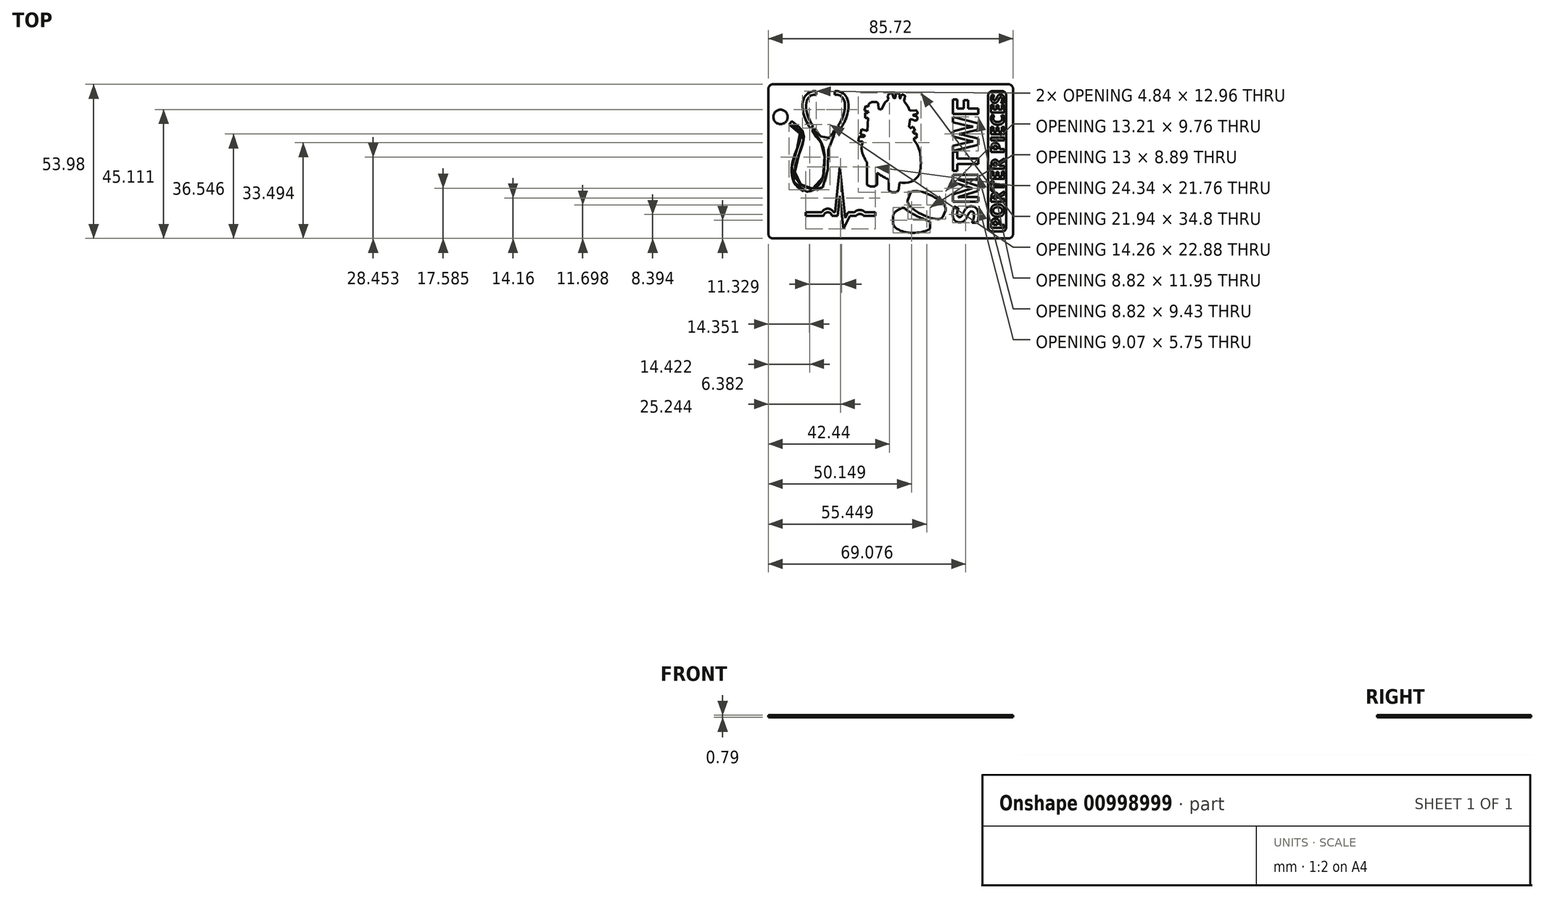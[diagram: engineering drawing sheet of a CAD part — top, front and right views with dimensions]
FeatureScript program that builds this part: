
annotation { "Feature Type Name" : "Feature", "Feature Type Description" : "" }
export const myFeature = defineFeature(function(context is Context, id is Id, definition is map)
    precondition{}
    {
        {
            var Q0;
            Q0=qCreatedBy(makeId("Top.planeOp"),FACE);
            var sketch = newSketch(context, id + "F0", { "sketchPlane" : qUnion([Q0])});
            skLineSegment(sketch, "E0.bottom", {"start": v(42.86, 26.99) * mm, "end": v(-42.86, 26.99) * mm});
            skLineSegment(sketch, "E0.top", {"start": v(42.86, -26.99) * mm, "end": v(-42.86, -26.99) * mm});
            skLineSegment(sketch, "E0.left", {"start": v(42.86, 26.99) * mm, "end": v(42.86, -26.99) * mm});
            skLineSegment(sketch, "E0.right", {"start": v(-42.86, 26.99) * mm, "end": v(-42.86, -26.99) * mm});
            skPoint(sketch, "E0.middle", {"position": v(0, 0) * mm});
            skSolve(sketch);
        }
        {
            var Q0;
            Q0=makeQuery(id+"F0.imprint","IMPRINT",FACE,{"disambiguationData":[TD([[makeQuery(id+"F0.imprint","IMPRINT",EDGE,{"derivedFrom":sQuery(id+"F0.wireOp",EDGE,"E0.bottom")}),1.0]])]});
            extrude(context, id + "F1", {"entities" : qUnion([Q0]), "depth" : 0.8 * mm, "offsetDistance" : 25.4 * mm});
        }
        {
            var Q0;
            Q0=makeQuery(id+"F1.opExtrude","SWEPT_EDGE",EDGE,{"disambiguationData":[OSD([sQuery(id+"F0.wireOp",EDGE,"E0.bottom"),sQuery(id+"F0.wireOp",EDGE,"E0.left")])]});
            var Q1;
            Q1=makeQuery(id+"F1.opExtrude","SWEPT_EDGE",EDGE,{"disambiguationData":[OSD([sQuery(id+"F0.wireOp",EDGE,"E0.bottom"),sQuery(id+"F0.wireOp",EDGE,"E0.right")])]});
            var Q2;
            Q2=makeQuery(id+"F1.opExtrude","SWEPT_EDGE",EDGE,{"disambiguationData":[OSD([sQuery(id+"F0.wireOp",EDGE,"E0.top"),sQuery(id+"F0.wireOp",EDGE,"E0.right")])]});
            var Q3;
            Q3=makeQuery(id+"F1.opExtrude","SWEPT_EDGE",EDGE,{"disambiguationData":[OSD([sQuery(id+"F0.wireOp",EDGE,"E0.top"),sQuery(id+"F0.wireOp",EDGE,"E0.left")])]});
            fillet(context, id + "F2", {"entities" : qUnion([Q0, Q1, Q2, Q3]), "radius" : 1.59 * mm, "tangentPropagation" : true, "allowEdgeOverflow" : false});
        }
        {
            var Q0;
            Q0=makeQuery(id+"F1.opExtrude","CAP_FACE",FACE,{"disambiguationData":[OSD([sQuery(id+"F0.wireOp",EDGE,"E0.bottom"),sQuery(id+"F0.wireOp",EDGE,"E0.top"),sQuery(id+"F0.wireOp",EDGE,"E0.left"),sQuery(id+"F0.wireOp",EDGE,"E0.right")])],"isStart":false});
            var sketch = newSketch(context, id + "F3", { "sketchPlane" : qUnion([Q0])});
            skLineSegment(sketch, "E1.bottom", {"start": v(34.13, -24.6) * mm, "end": v(40.48, -24.6) * mm});
            skLineSegment(sketch, "E1.top", {"start": v(34.13, 24.6) * mm, "end": v(40.48, 24.6) * mm});
            skLineSegment(sketch, "E1.left", {"start": v(34.13, -24.6) * mm, "end": v(34.13, 24.6) * mm});
            skLineSegment(sketch, "E1.right", {"start": v(40.48, -24.6) * mm, "end": v(40.48, 24.6) * mm});
            skSolve(sketch);
        }
        {
            var Q0;
            Q0=makeQuery(id+"F3.imprint","IMPRINT",FACE,{"disambiguationData":[TD([[makeQuery(id+"F3.imprint","IMPRINT",EDGE,{"derivedFrom":sQuery(id+"F3.wireOp",EDGE,"E1.bottom")}),1.0]])]});
            extrude(context, id + "F4", {"entities" : qUnion([Q0]), "operationType" : NewBodyOperationType.REMOVE, "oppositeDirection" : true, "depth" : 0.4 * mm, "offsetDistance" : 25.4 * mm});
        }
        {
            var Q0;
            Q0=makeQuery(id+"F4.boolean.opBoolean","COPY",EDGE,{"derivedFrom":makeQuery(id+"F4.opExtrude","SWEPT_EDGE",EDGE,{"disambiguationData":[OSD([sQuery(id+"F3.wireOp",EDGE,"E1.bottom"),sQuery(id+"F3.wireOp",EDGE,"E1.left")])]})});
            var Q1;
            Q1=makeQuery(id+"F4.boolean.opBoolean","COPY",EDGE,{"derivedFrom":makeQuery(id+"F4.opExtrude","SWEPT_EDGE",EDGE,{"disambiguationData":[OSD([sQuery(id+"F3.wireOp",EDGE,"E1.bottom"),sQuery(id+"F3.wireOp",EDGE,"E1.right")])]})});
            var Q2;
            Q2=makeQuery(id+"F4.boolean.opBoolean","COPY",EDGE,{"derivedFrom":makeQuery(id+"F4.opExtrude","SWEPT_EDGE",EDGE,{"disambiguationData":[OSD([sQuery(id+"F3.wireOp",EDGE,"E1.top"),sQuery(id+"F3.wireOp",EDGE,"E1.right")])]})});
            var Q3;
            Q3=makeQuery(id+"F4.boolean.opBoolean","COPY",EDGE,{"derivedFrom":makeQuery(id+"F4.opExtrude","SWEPT_EDGE",EDGE,{"disambiguationData":[OSD([sQuery(id+"F3.wireOp",EDGE,"E1.top"),sQuery(id+"F3.wireOp",EDGE,"E1.left")])]})});
            fillet(context, id + "F5", {"entities" : qUnion([Q0, Q1, Q2, Q3]), "radius" : 1.59 * mm, "tangentPropagation" : true, "allowEdgeOverflow" : false});
        }
        {
            var Q0;
            Q0=makeQuery(id+"F4.boolean.opBoolean","COPY",FACE,{"derivedFrom":makeQuery(id+"F4.opExtrude","CAP_FACE",FACE,{"disambiguationData":[OSD([sQuery(id+"F3.wireOp",EDGE,"E1.bottom"),sQuery(id+"F3.wireOp",EDGE,"E1.top"),sQuery(id+"F3.wireOp",EDGE,"E1.left"),sQuery(id+"F3.wireOp",EDGE,"E1.right")])],"isStart":false})});
            var sketch = newSketch(context, id + "F6", { "sketchPlane" : qUnion([Q0])});
            skText(sketch, "E2", { "text": "PORTER PIECES", "fontName": "OpenSans-Bold.ttf"});
            const initialGuessF6  = {"E2": [0.03976, -0.02381, 0, 1, 0.00461]};
            skSetInitialGuess(sketch, initialGuessF6);
            skSolve(sketch);
        }
        {
            var Q0;
            Q0=makeQuery(id+"F6.imprint","IMPRINT",FACE,{"disambiguationData":[TD([[makeQuery(id+"F6.imprint","IMPRINT",EDGE,{"derivedFrom":sQuery(id+"F6.wireOp",EDGE,"E2.sketch_text.stroke-0")}),-1.0]])]});
            var Q1;
            Q1=makeQuery(id+"F6.imprint","IMPRINT",FACE,{"disambiguationData":[TD([[makeQuery(id+"F6.imprint","IMPRINT",EDGE,{"derivedFrom":sQuery(id+"F6.wireOp",EDGE,"E2.sketch_text.stroke-16")}),-1.0]])]});
            var Q2;
            Q2=makeQuery(id+"F6.imprint","IMPRINT",FACE,{"disambiguationData":[TD([[makeQuery(id+"F6.imprint","IMPRINT",EDGE,{"derivedFrom":sQuery(id+"F6.wireOp",EDGE,"E2.sketch_text.stroke-30")}),-1.0]])]});
            var Q3;
            Q3=makeQuery(id+"F6.imprint","IMPRINT",FACE,{"disambiguationData":[TD([[makeQuery(id+"F6.imprint","IMPRINT",EDGE,{"derivedFrom":sQuery(id+"F6.wireOp",EDGE,"E2.sketch_text.stroke-49")}),-1.0]])]});
            var Q4;
            Q4=makeQuery(id+"F6.imprint","IMPRINT",FACE,{"disambiguationData":[TD([[makeQuery(id+"F6.imprint","IMPRINT",EDGE,{"derivedFrom":sQuery(id+"F6.wireOp",EDGE,"E2.sketch_text.stroke-57")}),-1.0]])]});
            var Q5;
            Q5=makeQuery(id+"F6.imprint","IMPRINT",FACE,{"disambiguationData":[TD([[makeQuery(id+"F6.imprint","IMPRINT",EDGE,{"derivedFrom":sQuery(id+"F6.wireOp",EDGE,"E2.sketch_text.stroke-69")}),-1.0]])]});
            var Q6;
            Q6=makeQuery(id+"F6.imprint","IMPRINT",FACE,{"disambiguationData":[TD([[makeQuery(id+"F6.imprint","IMPRINT",EDGE,{"derivedFrom":sQuery(id+"F6.wireOp",EDGE,"E2.sketch_text.stroke-88")}),-1.0]])]});
            var Q7;
            Q7=makeQuery(id+"F6.imprint","IMPRINT",FACE,{"disambiguationData":[TD([[makeQuery(id+"F6.imprint","IMPRINT",EDGE,{"derivedFrom":sQuery(id+"F6.wireOp",EDGE,"E2.sketch_text.stroke-104")}),-1.0]])]});
            var Q8;
            Q8=makeQuery(id+"F6.imprint","IMPRINT",FACE,{"disambiguationData":[TD([[makeQuery(id+"F6.imprint","IMPRINT",EDGE,{"derivedFrom":sQuery(id+"F6.wireOp",EDGE,"E2.sketch_text.stroke-108")}),-1.0]])]});
            var Q9;
            Q9=makeQuery(id+"F6.imprint","IMPRINT",FACE,{"disambiguationData":[TD([[makeQuery(id+"F6.imprint","IMPRINT",EDGE,{"derivedFrom":sQuery(id+"F6.wireOp",EDGE,"E2.sketch_text.stroke-120")}),-1.0]])]});
            var Q10;
            Q10=makeQuery(id+"F6.imprint","IMPRINT",FACE,{"disambiguationData":[TD([[makeQuery(id+"F6.imprint","IMPRINT",EDGE,{"derivedFrom":sQuery(id+"F6.wireOp",EDGE,"E2.sketch_text.stroke-135")}),-1.0]])]});
            var Q11;
            Q11=makeQuery(id+"F6.imprint","IMPRINT",FACE,{"disambiguationData":[TD([[makeQuery(id+"F6.imprint","IMPRINT",EDGE,{"derivedFrom":sQuery(id+"F6.wireOp",EDGE,"E2.sketch_text.stroke-147")}),-1.0]])]});
            extrude(context, id + "F7", {"entities" : qUnion([Q0, Q1, Q2, Q3, Q4, Q5, Q6, Q7, Q8, Q9, Q10, Q11]), "operationType" : NewBodyOperationType.ADD, "depth" : 0.4 * mm, "offsetDistance" : 25.4 * mm});
        }
        {
            var Q0;
            Q0=makeQuery(id+"F1.opExtrude","CAP_FACE",FACE,{"disambiguationData":[OSD([sQuery(id+"F0.wireOp",EDGE,"E0.bottom"),sQuery(id+"F0.wireOp",EDGE,"E0.top"),sQuery(id+"F0.wireOp",EDGE,"E0.left"),sQuery(id+"F0.wireOp",EDGE,"E0.right")])],"isStart":false});
            var sketch = newSketch(context, id + "F8", { "sketchPlane" : qUnion([Q0])});
            skFitSpline(sketch, "E3", {"points": [v(-4.35, 20.18) * mm, v(-4.76, 20.65) * mm, v(-6.04, 20.8) * mm, v(-7.15, 20.5) * mm, v(-7.75, 19.93) * mm], "startDerivative": vector(-1.5, 2.67) * mm, "endDerivative": vector(-2.26, -2.76) * mm});
            skLineSegment(sketch, "E4", {"start": v(-7.75, 19.93) * mm, "end": v(-7.78, 19.11) * mm});
            skLineSegment(sketch, "E5", {"start": v(-4.35, 20.18) * mm, "end": v(-4.23, 18.33) * mm});
            skFitSpline(sketch, "E6", {"points": [v(-3.88, 11.67) * mm, v(-1.48, 21.19) * mm, v(-0.82, 21.64) * mm, v(-0.95, 23.44) * mm, v(0.63, 23.68) * mm, v(0.82, 22.6) * mm, v(1.36, 22.06) * mm, v(1.75, 22.6) * mm, v(1.7, 23.78) * mm, v(2.97, 23.68) * mm, v(3.02, 22.95) * mm, v(3.31, 21.97) * mm, v(3.7, 23.34) * mm, v(5.02, 22.91) * mm, v(4.72, 21.55) * mm, v(5.16, 20.36) * mm, v(6.52, 16.52) * mm, v(-3.88, 11.67) * mm]});
            skLineSegment(sketch, "E7", {"start": v(6.7, 17.75) * mm, "end": v(8.84, 17.9) * mm});
            skFitSpline(sketch, "E8", {"points": [v(8.84, 17.9) * mm, v(9.35, 17.37) * mm, v(9.29, 16.67) * mm, v(7.8, 16.22) * mm, v(9.01, 15.73) * mm, v(9.36, 15.03) * mm, v(8.84, 14.3) * mm, v(6.86, 14.82) * mm, v(5.42, 14.7) * mm, v(0.6, 14.8) * mm, v(0.51, 15.09) * mm, v(0.51, 16.3) * mm, v(1.62, 17.4) * mm], "startDerivative": vector(9.11, -7.18) * mm, "endDerivative": vector(15.7, 10.5) * mm});
            skFitSpline(sketch, "E9.trimOffspring", {"points": [v(-3.28, 12.6) * mm, v(-4.3, 12.92) * mm, v(-6.2, 12.39) * mm, v(-8.38, 10.3) * mm, v(-9.82, 6.92) * mm, v(-10.15, 3.95) * mm, v(-9.57, 2.02) * mm, v(-8, -0.45) * mm, v(-7.43, -0.4) * mm, v(-7.43, -1.27) * mm, v(-5.66, -3.33) * mm, v(-2.9, -5.22) * mm, v(0.43, -6.78) * mm, v(4.05, -7.53) * mm, v(7.75, -6.9) * mm, v(10.1, -4.15) * mm, v(10.55, -0.24) * mm, v(10.18, 3.34) * mm, v(8.78, 6.55) * mm, v(8.2, 7.33) * mm, v(8.29, 8.6) * mm, v(7.75, 10.46) * mm, v(5.82, 12.8) * mm, v(4.63, 13.55) * mm], "startDerivative": vector(-31.36, 17.68) * mm, "endDerivative": vector(-41.94, 14.95) * mm});
            skLineSegment(sketch, "E10", {"start": v(-8.33, -0.24) * mm, "end": v(-8.33, -8.18) * mm});
            skArc(sketch, "E11", {"start": v(-8.33, -8.18) * mm, "mid": v(-6.51, -8.87) * mm, "end": v(-4.7, -8.18) * mm});
            skLineSegment(sketch, "E12", {"start": v(-4.7, -8.18) * mm, "end": v(-4.7, -4.05) * mm});
            skLineSegment(sketch, "E13", {"start": v(-0.63, -6.37) * mm, "end": v(-0.63, -10.2) * mm});
            skArc(sketch, "E14", {"start": v(-0.63, -10.2) * mm, "mid": v(1.08, -10.9) * mm, "end": v(2.79, -10.2) * mm});
            skLineSegment(sketch, "E15", {"start": v(2.79, -10.2) * mm, "end": v(3.06, -7.43) * mm});
            skLineSegment(sketch, "E16", {"start": v(6.86, 14.82) * mm, "end": v(6.48, 12.13) * mm});
            skLineSegment(sketch, "E17", {"start": v(-3.27, 18.12) * mm, "end": v(-4.23, 18.33) * mm});
            skLineSegment(sketch, "E18", {"start": v(-8.82, 19.34) * mm, "end": v(-9.16, 17.78) * mm});
            skLineSegment(sketch, "E19", {"start": v(-9.16, 17.78) * mm, "end": v(-7.86, 17.5) * mm});
            skLineSegment(sketch, "E20", {"start": v(-7.88, 16.96) * mm, "end": v(-9, 17.01) * mm});
            skLineSegment(sketch, "E21", {"start": v(-9, 17.01) * mm, "end": v(-9, 15.25) * mm});
            skLineSegment(sketch, "E22", {"start": v(-9, 15.25) * mm, "end": v(-7.96, 15.25) * mm});
            skLineSegment(sketch, "E23.trimOffspring", {"start": v(-7.78, 19.11) * mm, "end": v(-8.82, 19.34) * mm});
            skLineSegment(sketch, "E24.trimOffspring", {"start": v(-7.86, 17.5) * mm, "end": v(-7.88, 16.96) * mm});
            skLineSegment(sketch, "E25.trimOffspring", {"start": v(-7.96, 15.25) * mm, "end": v(-8.17, 10.58) * mm});
            skLineSegment(sketch, "E26", {"start": v(-8.17, 10.58) * mm, "end": v(-10.24, 11.24) * mm});
            skLineSegment(sketch, "E27", {"start": v(-10.24, 11.24) * mm, "end": v(-10.63, 9.47) * mm});
            skLineSegment(sketch, "E28", {"start": v(-10.63, 9.47) * mm, "end": v(-9.04, 9.12) * mm});
            skLineSegment(sketch, "E29", {"start": v(-9.24, 8.66) * mm, "end": v(-11.05, 8.66) * mm});
            skLineSegment(sketch, "E30", {"start": v(-11.05, 8.66) * mm, "end": v(-11.4, 7.11) * mm});
            skLineSegment(sketch, "E31", {"start": v(-11.4, 7.11) * mm, "end": v(-9.81, 6.94) * mm});
            skPoint(sketch, "E32.orphan", {"position": v(-9.62, 6.92) * mm});
            skLineSegment(sketch, "E33", {"start": v(6.95, 11.58) * mm, "end": v(7.88, 12.16) * mm});
            skLineSegment(sketch, "E34", {"start": v(7.88, 12.16) * mm, "end": v(8.6, 10.73) * mm});
            skLineSegment(sketch, "E35", {"start": v(8.6, 10.73) * mm, "end": v(7.75, 10.46) * mm});
            skLineSegment(sketch, "E36", {"start": v(8.1, 9.7) * mm, "end": v(9.14, 9.7) * mm});
            skLineSegment(sketch, "E37", {"start": v(9.14, 9.7) * mm, "end": v(9.14, 8.17) * mm});
            skLineSegment(sketch, "E38", {"start": v(9.14, 8.17) * mm, "end": v(8.24, 8.17) * mm});
            skSolve(sketch);
        }
        {
            var Q0;
            Q0 = qSketchRegion(id + "F8", true);
            extrude(context, id + "F9", {"entities" : qUnion([Q0]), "operationType" : NewBodyOperationType.REMOVE, "oppositeDirection" : true, "depth" : 25.4 * mm, "offsetDistance" : 25.4 * mm});
        }
        {
            var Q0;
            Q0=makeQuery(id+"F1.opExtrude","CAP_FACE",FACE,{"disambiguationData":[OSD([sQuery(id+"F0.wireOp",EDGE,"E0.bottom"),sQuery(id+"F0.wireOp",EDGE,"E0.top"),sQuery(id+"F0.wireOp",EDGE,"E0.left"),sQuery(id+"F0.wireOp",EDGE,"E0.right")])],"isStart":false});
            var sketch = newSketch(context, id + "F10", { "sketchPlane" : qUnion([Q0])});
            skLineSegment(sketch, "E39", {"start": v(-29.79, -19.14) * mm, "end": v(-23.5, -19.14) * mm});
            skArc(sketch, "E40", {"start": v(-20.58, -19.14) * mm, "mid": v(-22.04, -17.85) * mm, "end": v(-23.5, -19.14) * mm});
            skLineSegment(sketch, "E41", {"start": v(-20.58, -19.14) * mm, "end": v(-18.55, -19.14) * mm});
            skLineSegment(sketch, "E42", {"start": v(-18.55, -19.14) * mm, "end": v(-17.85, -12.1) * mm});
            skLineSegment(sketch, "E43", {"start": v(-17.85, -12.1) * mm, "end": v(-16.61, -23.7) * mm});
            skLineSegment(sketch, "E44", {"start": v(-16.61, -23.7) * mm, "end": v(-14.28, -19.14) * mm});
            skArc(sketch, "E45", {"start": v(-9.49, -19.14) * mm, "mid": v(-10.8, -18.4) * mm, "end": v(-12.1, -19.14) * mm});
            skLineSegment(sketch, "E46", {"start": v(-9.49, -19.14) * mm, "end": v(-5.45, -19.14) * mm});
            skLineSegment(sketch, "E47.0", {"start": v(-8.96, -17.87) * mm, "end": v(-5.45, -17.87) * mm});
            skArc(sketch, "E47.1", {"start": v(-8.96, -17.87) * mm, "mid": v(-10.84, -17.03) * mm, "end": v(-12.72, -17.87) * mm});
            skLineSegment(sketch, "E47.3", {"start": v(-17.88, -1.95) * mm, "end": v(-15.97, -19.9) * mm});
            skLineSegment(sketch, "E47.4", {"start": v(-29.79, -17.87) * mm, "end": v(-24.1, -17.87) * mm});
            skArc(sketch, "E47.5", {"start": v(-19.99, -17.87) * mm, "mid": v(-22.04, -16.58) * mm, "end": v(-24.1, -17.87) * mm});
            skLineSegment(sketch, "E47.6", {"start": v(-19.99, -17.87) * mm, "end": v(-19.46, -17.87) * mm});
            skLineSegment(sketch, "E47.7", {"start": v(-19.46, -17.87) * mm, "end": v(-17.88, -1.95) * mm});
            skLineSegment(sketch, "E48.trimOffspring", {"start": v(-15.97, -19.9) * mm, "end": v(-14.88, -17.87) * mm});
            skLineSegment(sketch, "E49", {"start": v(-12.72, -17.87) * mm, "end": v(-14.88, -17.87) * mm});
            skLineSegment(sketch, "E50", {"start": v(-12.1, -19.14) * mm, "end": v(-14.28, -19.14) * mm});
            skLineSegment(sketch, "E51", {"start": v(-29.79, -17.87) * mm, "end": v(-29.79, -19.14) * mm});
            skLineSegment(sketch, "E52", {"start": v(-5.45, -19.14) * mm, "end": v(-5.45, -17.87) * mm});
            skSolve(sketch);
        }
        {
            var Q0;
            Q0 = qSketchRegion(id + "F10", true);
            extrude(context, id + "F11", {"entities" : qUnion([Q0]), "operationType" : NewBodyOperationType.REMOVE, "oppositeDirection" : true, "depth" : 25.4 * mm, "offsetDistance" : 25.4 * mm});
        }
        {
            var Q0;
            Q0=makeQuery(id+"F1.opExtrude","CAP_FACE",FACE,{"disambiguationData":[OSD([sQuery(id+"F0.wireOp",EDGE,"E0.bottom"),sQuery(id+"F0.wireOp",EDGE,"E0.top"),sQuery(id+"F0.wireOp",EDGE,"E0.left"),sQuery(id+"F0.wireOp",EDGE,"E0.right")])],"isStart":false});
            var sketch = newSketch(context, id + "F12", { "sketchPlane" : qUnion([Q0])});
            skFitSpline(sketch, "E53", {"points": [v(-35.57, 12.9) * mm, v(-34.97, 14.01) * mm, v(-32.68, 12.56) * mm, v(-30.89, 10.6) * mm, v(-30.47, 8.38) * mm, v(-30.95, 5.4) * mm, v(-32, 2.75) * mm, v(-33.33, -1.04) * mm, v(-33.56, -4.15) * mm, v(-32.84, -6.51) * mm, v(-31.54, -8.13) * mm, v(-30.1, -9.06) * mm, v(-27.87, -9.55) * mm, v(-25.34, -8.64) * mm, v(-23.71, -5.4) * mm, v(-23.17, -0.1) * mm, v(-23.35, 3.58) * mm, v(-23.9, 5.8) * mm, v(-25.58, 8.1) * mm, v(-27.45, 10.92) * mm, v(-26.66, 11.59) * mm, v(-25.22, 9.84) * mm, v(-24.32, 8.52) * mm, v(-23.47, 7.55) * mm, v(-22.27, 7.55) * mm, v(-21.25, 8.88) * mm, v(-20.22, 10.58) * mm, v(-19.43, 11.34) * mm, v(-18.6, 10.68) * mm, v(-19.38, 9.18) * mm, v(-20.76, 7.2) * mm, v(-21.67, 5.57) * mm, v(-21.85, 3.94) * mm, v(-21.9, -0.21) * mm, v(-22.33, -4.73) * mm, v(-23.47, -8.52) * mm, v(-25.94, -10.5) * mm, v(-29.83, -10.6) * mm, v(-32.83, -8.84) * mm, v(-34.25, -6.25) * mm, v(-34.73, -3.14) * mm, v(-34.31, 0.2) * mm, v(-33.05, 3.82) * mm, v(-31.84, 7.01) * mm, v(-31.84, 9.84) * mm, v(-33.53, 11.83) * mm, v(-35.57, 12.9) * mm]});
            skCircle(sketch, "E54", {"center": v(-38.6, 15.57) * mm, "radius": 2.52 * mm});
            skFitSpline(sketch, "E55.0", {"points": [v(-26.13, 24.6) * mm, v(-26.4, 24.6) * mm, v(-26.84, 24.58) * mm, v(-27.47, 24.5) * mm, v(-27.95, 24.37) * mm, v(-28.44, 24.17) * mm, v(-28.91, 23.9) * mm, v(-29.35, 23.55) * mm, v(-29.75, 23.14) * mm, v(-30.1, 22.66) * mm, v(-30.46, 21.95) * mm, v(-30.76, 21) * mm, v(-30.92, 19.85) * mm, v(-30.9, 18.79) * mm, v(-30.77, 17.8) * mm, v(-30.58, 16.86) * mm, v(-30.37, 16.04) * mm, v(-30.14, 15.36) * mm, v(-29.87, 14.66) * mm, v(-29.45, 13.75) * mm, v(-29, 12.93) * mm, v(-28.69, 12.4) * mm, v(-28.4, 11.99) * mm, v(-28.23, 11.77) * mm, v(-28.12, 11.64) * mm]});
            skFitSpline(sketch, "E56.0", {"points": [v(-26.09, 23.35) * mm, v(-26.37, 23.34) * mm, v(-26.76, 23.33) * mm, v(-27.23, 23.26) * mm, v(-27.56, 23.18) * mm, v(-27.88, 23.04) * mm, v(-28.31, 22.8) * mm, v(-28.7, 22.44) * mm, v(-29.02, 22) * mm, v(-29.3, 21.5) * mm, v(-29.53, 20.74) * mm, v(-29.66, 19.78) * mm, v(-29.65, 18.89) * mm, v(-29.56, 18.16) * mm, v(-29.45, 17.57) * mm, v(-29.32, 16.98) * mm, v(-29.13, 16.25) * mm, v(-28.8, 15.33) * mm, v(-28.4, 14.48) * mm, v(-28.08, 13.85) * mm, v(-27.84, 13.43) * mm, v(-27.63, 13.08) * mm, v(-27.46, 12.82) * mm, v(-27.3, 12.62) * mm, v(-27.2, 12.5) * mm, v(-27.15, 12.43) * mm]});
            skLineSegment(sketch, "E57", {"start": v(-26.13, 24.6) * mm, "end": v(-26.09, 23.35) * mm});
            skLineSegment(sketch, "E58", {"start": v(-27.15, 12.43) * mm, "end": v(-28.12, 11.64) * mm});
            skLineSegment(sketch, "E59.MirrorCS", {"start": v(-19.56, 24.6) * mm, "end": v(-19.6, 23.35) * mm});
            skLineSegment(sketch, "E60.MirrorCS", {"start": v(-18.54, 12.43) * mm, "end": v(-17.57, 11.64) * mm});
            skFitSpline(sketch, "E61.MirrorCS", {"points": [v(-19.56, 24.6) * mm, v(-19.29, 24.6) * mm, v(-18.85, 24.58) * mm, v(-18.22, 24.5) * mm, v(-17.74, 24.37) * mm, v(-17.24, 24.17) * mm, v(-16.78, 23.9) * mm, v(-16.34, 23.55) * mm, v(-15.94, 23.14) * mm, v(-15.6, 22.66) * mm, v(-15.23, 21.95) * mm, v(-14.93, 21) * mm, v(-14.77, 19.85) * mm, v(-14.79, 18.79) * mm, v(-14.92, 17.8) * mm, v(-15.1, 16.86) * mm, v(-15.32, 16.04) * mm, v(-15.54, 15.36) * mm, v(-15.82, 14.66) * mm, v(-16.24, 13.75) * mm, v(-16.68, 12.93) * mm, v(-17, 12.4) * mm, v(-17.28, 11.99) * mm, v(-17.46, 11.77) * mm, v(-17.57, 11.64) * mm]});
            skFitSpline(sketch, "E62.MirrorCS", {"points": [v(-19.6, 23.35) * mm, v(-19.32, 23.34) * mm, v(-18.93, 23.33) * mm, v(-18.46, 23.26) * mm, v(-18.13, 23.18) * mm, v(-17.8, 23.04) * mm, v(-17.38, 22.8) * mm, v(-16.98, 22.44) * mm, v(-16.67, 22) * mm, v(-16.4, 21.5) * mm, v(-16.16, 20.74) * mm, v(-16.02, 19.78) * mm, v(-16.04, 18.89) * mm, v(-16.13, 18.16) * mm, v(-16.24, 17.57) * mm, v(-16.37, 16.98) * mm, v(-16.56, 16.25) * mm, v(-16.89, 15.33) * mm, v(-17.28, 14.48) * mm, v(-17.6, 13.85) * mm, v(-17.84, 13.43) * mm, v(-18.06, 13.08) * mm, v(-18.23, 12.82) * mm, v(-18.38, 12.62) * mm, v(-18.48, 12.5) * mm, v(-18.54, 12.43) * mm]});
            skSolve(sketch);
        }
        {
            var Q0;
            Q0 = qSketchRegion(id + "F12", true);
            extrude(context, id + "F13", {"entities" : qUnion([Q0]), "operationType" : NewBodyOperationType.REMOVE, "oppositeDirection" : true, "depth" : 25.4 * mm, "offsetDistance" : 25.4 * mm});
        }
        {
            var Q0;
            Q0=makeQuery(id+"F8.imprint","IMPRINT",FACE,{"disambiguationData":[TD([[makeQuery(id+"F8.imprint","IMPRINT",EDGE,{"derivedFrom":sQuery(id+"F8.wireOp",EDGE,"E3")}),-1.0]])]});
            var sketch = newSketch(context, id + "F14", { "sketchPlane" : qUnion([Q0])});
            skEllipticalArc(sketch, "E63", {});
            skEllipticalArc(sketch, "E64", {});
            skEllipticalArc(sketch, "E65", {});
            skLineSegment(sketch, "E66", {"start": v(7, -11.07) * mm, "end": v(5.99, -13.42) * mm});
            skLineSegment(sketch, "E67", {"start": v(19.2, -17.16) * mm, "end": v(18.17, -19.52) * mm});
            skEllipticalArc(sketch, "E68", {});
            skLineSegment(sketch, "E69", {"start": v(0.85, -19.3) * mm, "end": v(0.79, -21.52) * mm});
            skEllipticalArc(sketch, "E70", {});
            skLineSegment(sketch, "E71", {"start": v(13.79, -21.1) * mm, "end": v(13.79, -23.56) * mm});
            const initialGuessF14  = {"E63": [0.013099424472003313, -0.0141121147659698, 0.8944272632938565, -0.44721345091204784, 0.006812285611503152, 0.0024209869565803848, 0, 3.1808995137074905], "E64": [0.008072622803430532, -0.01929124267585356, -1, 0, 0.007220406837253359, 0.0035625390248999996, 5.210906971735147, 0], "E65": [0.01207849514550971, -0.01647142194608226, 0.8944272632938549, -0.44721345091205095, 0.006812285611503152, 0.0024209869565803848, 3.141592653589793, 0.03930686011767118], "E68": [0.007947897998247175, -0.02152033382029249, -1, 0, 0.007159386283972939, 0.003532431565960029, 0, 2.52493995922794], "E70": [0.011924999316529766, -0.01898282279758326, 0.9203874171211344, -0.39100767563449085, 0.007991562744494892, 0.0012846464275488405, 3.345538485905865, 5.03613392097985]};
            skSetInitialGuess(sketch, initialGuessF14);
            skSolve(sketch);
        }
        {
            var Q0;
            Q0 = qSketchRegion(id + "F14", true);
            extrude(context, id + "F15", {"entities" : qUnion([Q0]), "operationType" : NewBodyOperationType.REMOVE, "oppositeDirection" : true, "depth" : 25.4 * mm, "offsetDistance" : 25.4 * mm});
        }
        {
            var Q0;
            Q0=makeQuery(id+"F8.imprint","IMPRINT",FACE,{"disambiguationData":[TD([[makeQuery(id+"F8.imprint","IMPRINT",EDGE,{"derivedFrom":sQuery(id+"F8.wireOp",EDGE,"E3")}),-1.0]])]});
            var sketch = newSketch(context, id + "F16", { "sketchPlane" : qUnion([Q0])});
            skText(sketch, "E72", { "text": "SMTWF", "fontName": "OpenSans-Bold.ttf"});
            const initialGuessF16  = {"E72": [0.03063, -0.02204, 0, 1, 0.0089]};
            skSetInitialGuess(sketch, initialGuessF16);
            skSolve(sketch);
        }
        {
            var Q0;
            Q0 = qSketchRegion(id + "F16", true);
            extrude(context, id + "F17", {"entities" : qUnion([Q0]), "operationType" : NewBodyOperationType.REMOVE, "oppositeDirection" : true, "depth" : 25.4 * mm, "offsetDistance" : 25.4 * mm});
        }
    });
